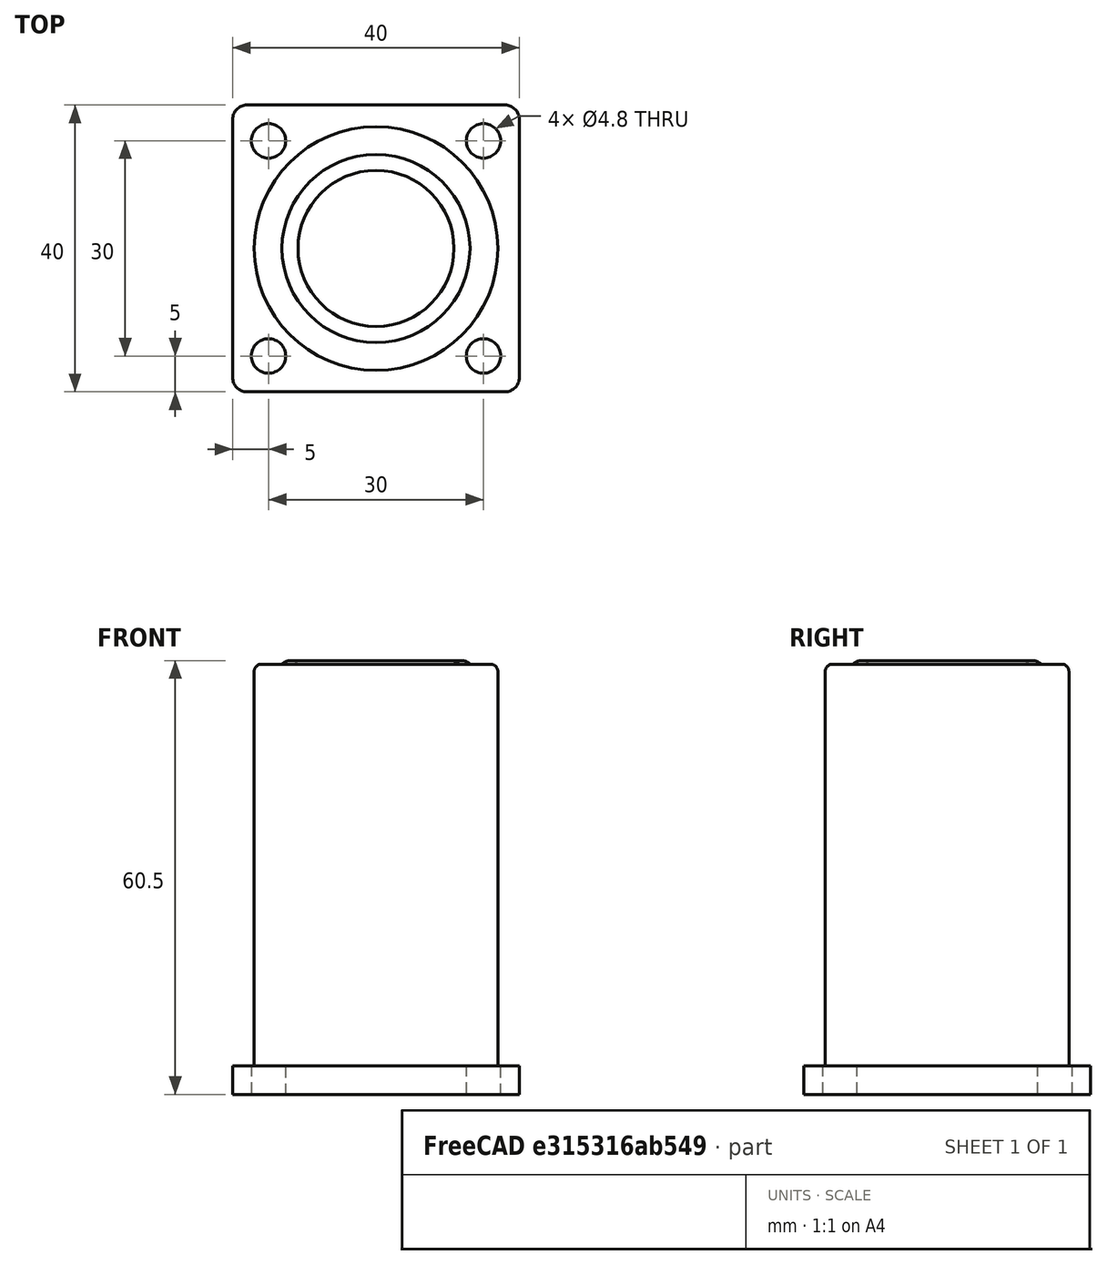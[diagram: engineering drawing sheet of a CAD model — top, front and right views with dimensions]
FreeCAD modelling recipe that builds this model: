
FCSTD DOCUMENT  (FreeCAD 1.0R39319 (Git))
Label: ojt1_t15r03_table_leg
License: All rights reserved
LicenseURL: https://en.wikipedia.org/wiki/All_rights_reserved
objects: Part::Cylinder×5, Part::MultiFuse×4, Part::Fillet×3, Part::Cut×2, Part::Box×1, Part::Torus×1
note: 16 computed .brp shape members not serialized (recipe doc carries the construction recipe); baked Part::Feature solids carry a one-line shape summary decoded from their .brp

FEATURE [Part::Box] Box  label="Cube"
  AttacherType = Attacher::AttachEngine3D
  Height = 4
  Length = 40
  Width = 40
FEATURE [Part::Fillet] Fillet
  Base = -> Box
  EdgeLinks = -> Box [Edge1,Edge3,Edge5,Edge7]
  Edges = 4 edges r=2: [Edge1,Edge3,Edge5,Edge7]
FEATURE [Part::Cylinder] Cylinder
  Angle = 360
  AttacherType = Attacher::AttachEngine3D
  FirstAngle = 0
  Height = 10
  Placement = pos=(5,5,0) rot=(0,0,1;0rad)
  Radius = 2.4
  SecondAngle = 0
FEATURE [Part::Cylinder] Cylinder001
  Angle = 360
  AttacherType = Attacher::AttachEngine3D
  FirstAngle = 0
  Height = 10
  Placement = pos=(5,35,0) rot=(0,0,1;0rad)
  Radius = 2.4
  SecondAngle = 0
FEATURE [Part::MultiFuse] Fusion
  Refine = true
  Shapes = -> [Cylinder001,Cylinder]
FEATURE [Part::Cylinder] Cylinder002
  Angle = 360
  AttacherType = Attacher::AttachEngine3D
  FirstAngle = 0
  Height = 10
  Placement = pos=(5,5,0) rot=(0,0,1;0rad)
  Radius = 2.4
  SecondAngle = 0
FEATURE [Part::Cylinder] Cylinder003
  Angle = 360
  AttacherType = Attacher::AttachEngine3D
  FirstAngle = 0
  Height = 10
  Placement = pos=(5,35,0) rot=(0,0,1;0rad)
  Radius = 2.4
  SecondAngle = 0
FEATURE [Part::MultiFuse] Fusion001
  Placement = pos=(30,0,0) rot=(0,0,1;0rad)
  Refine = true
  Shapes = -> [Cylinder003,Cylinder002]
FEATURE [Part::MultiFuse] Fusion002
  Refine = true
  Shapes = -> [Fusion001,Fusion]
FEATURE [Part::Cut] Cut
  Base = -> Fillet
  Refine = true
  Tool = -> Fusion002
FEATURE [Part::Cylinder] Cylinder004
  Angle = 360
  AttacherType = Attacher::AttachEngine3D
  FirstAngle = 0
  Height = 60
  Placement = pos=(20,20,0) rot=(0,0,1;0rad)
  Radius = 17
  SecondAngle = 0
FEATURE [Part::Fillet] Fillet001
  Base = -> Cylinder004
  EdgeLinks = -> Cylinder004 [Edge3]
  Edges = 1 edges r=1: [Edge3]
FEATURE [Part::Torus] Torus
  Angle1 = -180
  Angle2 = 180
  Angle3 = 360
  AttacherType = Attacher::AttachEngine3D
  Placement = pos=(20,20,59) rot=(0,0,1;0rad)
  Radius1 = 12
  Radius2 = 1.5
FEATURE [Part::Cut] Cut001
  Base = -> Torus
  Refine = true
  Tool = -> Fillet001
FEATURE [Part::Fillet] Fillet002
  Base = -> Cylinder004
  EdgeLinks = -> Cylinder004 [Edge3]
  Edges = 1 edges r=1: [Edge3]
FEATURE [Part::MultiFuse] Fusion003
  Refine = true
  Shapes = -> [Fillet002,Cut001,Cut]
